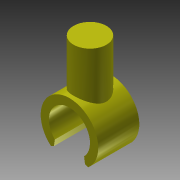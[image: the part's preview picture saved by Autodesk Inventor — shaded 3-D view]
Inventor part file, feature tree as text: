
AUTODESK INVENTOR PART (.ipt)
format: ipt  version: 2015 (Build 190159000, 159)  size: 116,736 bytes
history: native  units: mm
features: extrude x2, sketch x2, chamfer x1, plane x1
ambient origin geometry x8: Origin, YZ Plane, XZ Plane, XY Plane, X Axis, Y Axis, Z Axis, Center Point
bodies: Solid1 (feature_tree)
feature tree (6):
  extrude  "Extrusion1"  Depth=2.5mm
  chamfer  "Chamfer1"  Distance=1.78mm
  plane  "Work Plane1"
  extrude  "Extrusion2"  Depth=4.436mm TaperAngle=0.0deg
  sketch  "Sketch1"  dims[d0=3.5mm d1=2.5mm]
  sketch  "Sketch2"  dims[d2=1.95mm d3=1.78mm d4=2.5mm d5=0.0mm d6=0.2mm d7=2.0mm d8=45.0deg d9=4.436mm d10=2.0mm d11=2.5mm d12=0.0mm]
